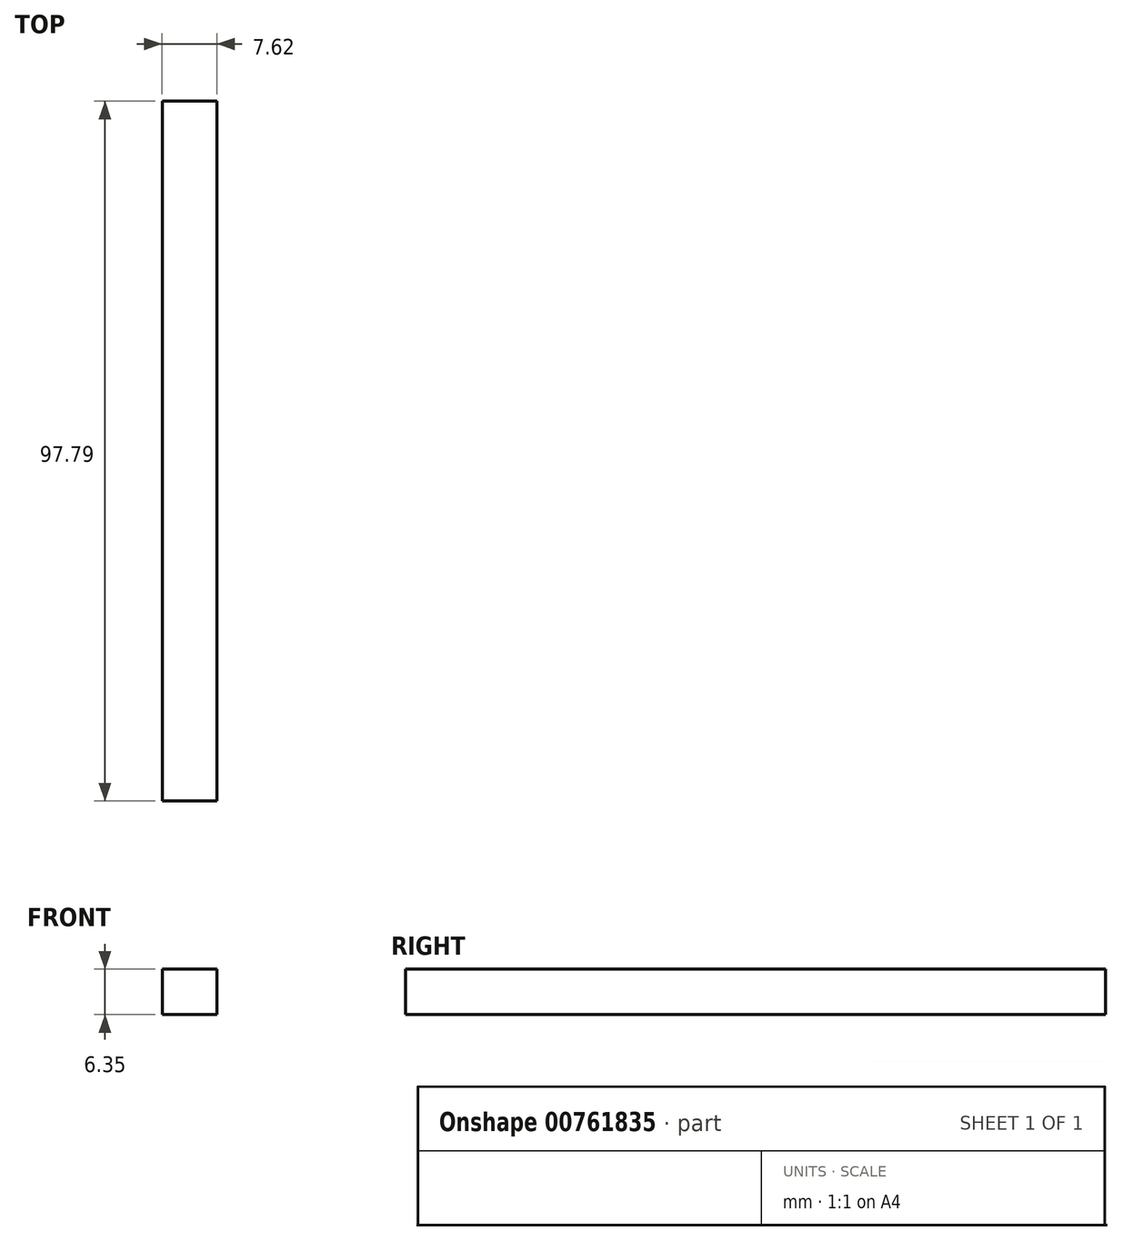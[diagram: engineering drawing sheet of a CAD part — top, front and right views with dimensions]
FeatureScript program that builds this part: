
annotation { "Feature Type Name" : "Feature", "Feature Type Description" : "" }
export const myFeature = defineFeature(function(context is Context, id is Id, definition is map)
    precondition{}
    {
        {
            var Q0;
            Q0=qCreatedBy(makeId("Top.planeOp"),FACE);
            var sketch = newSketch(context, id + "F0", { "sketchPlane" : qUnion([Q0])});
            skLineSegment(sketch, "E0.bottom", {"start": v(-20.05, 97.93) * mm, "end": v(-12.43, 97.93) * mm});
            skLineSegment(sketch, "E0.top", {"start": v(-20.05, 0.14) * mm, "end": v(-12.43, 0.14) * mm});
            skLineSegment(sketch, "E0.left", {"start": v(-20.05, 97.93) * mm, "end": v(-20.05, 0.14) * mm});
            skLineSegment(sketch, "E0.right", {"start": v(-12.43, 97.93) * mm, "end": v(-12.43, 0.14) * mm});
            skSolve(sketch);
        }
        {
            var Q0;
            Q0=makeQuery(id+"F0.imprint","IMPRINT",FACE,{"disambiguationData":[TD([[makeQuery(id+"F0.imprint","IMPRINT",EDGE,{"derivedFrom":sQuery(id+"F0.wireOp",EDGE,"E0.bottom")}),-1.0]])]});
            extrude(context, id + "F1", {"entities" : qUnion([Q0]), "depth" : 6.35 * mm, "offsetDistance" : 25.4 * mm});
        }
    });
